# Revit family: S-757
name_source: partatom
category: Aparatos sanitarios
revit_build: Autodesk Revit 2015 (Build: 20140606_1530(x64)
units: mm (PartAtom-declared; Revit-internal decimal feet)

## types (12) — shared parameters
B = 52 mm
Comentarios de tipo = COMPATIBLE CON CERCOS VISTOS Y OCULTOS
Fabricante = Jimten
Modelo = S-757
URL = http://www.jimten.com

## per-type parameters (varying)
| type | A | Descripción | Material | Medida | Referencia | Rejilla |
| 50x350mm_CRYSTAL NEGRO | 340 mm  [stored 1.11549 ft] | REJILLA PARA CANALETA, CRYSTAL NEGRO, PARA CANALETA ANCHO 50 | Cristal templado (Negro) | 350mm x 50mm | 13533 | Cristal templado (Negro) |
| 50x550mm_CRYSTAL NEGRO | 540 mm  [stored 1.77165 ft] | REJILLA PARA CANALETA, CRYSTAL NEGRO, PARA CANALETA ANCHO 50 | Cristal templado (Negro) | 550mm x 50mm | 13553 | Cristal templado (Negro) |
| 50x650mm_CRYSTAL NEGRO | 640 mm  [stored 2.09974 ft] | REJILLA PARA CANALETA, CRYSTAL NEGRO, PARA CANALETA ANCHO 50 | Cristal templado (Negro) | 650mm x 50mm | 13563 | Cristal templado (Negro) |
| 50x750mm_CRYSTAL NEGRO | 740 mm  [stored 2.42782 ft] | REJILLA PARA CANALETA, CRYSTAL NEGRO, PARA CANALETA ANCHO 50 | Cristal templado (Negro) | 750mm x 50mm | 13573 | Cristal templado (Negro) |
| 50x850mm_CRYSTAL NEGRO | 840 mm  [stored 2.75591 ft] | REJILLA PARA CANALETA, CRYSTAL NEGRO, PARA CANALETA ANCHO 50 | Cristal templado (Negro) | 850mm x 50mm | 13583 | Cristal templado (Negro) |
| 50x950mm_CRYSTAL NEGRO | 940 mm  [stored 3.08399 ft] | REJILLA PARA CANALETA, CRYSTAL NEGRO, PARA CANALETA ANCHO 50 | Cristal templado (Negro) | 950mm x 50mm | 13593 | Cristal templado (Negro) |
| 50x350mm_CRYSTAL BLANCO | 340 mm  [stored 1.11549 ft] | REJILLA PARA CANALETA, CRYSTAL BLANCO, PARA CANALETA ANCHO 50 | Cristal templado (Blanco) | 350mm x 50mm | 13534 | Cristal templado (Blanco) |
| 50x550mm_CRYSTAL BLANCO | 540 mm  [stored 1.77165 ft] | REJILLA PARA CANALETA, CRYSTAL BLANCO, PARA CANALETA ANCHO 50 | Cristal templado (Blanco) | 550mm x 50mm | 13554 | Cristal templado (Blanco) |
| 50x650mm_CRYSTAL BLANCO | 640 mm  [stored 2.09974 ft] | REJILLA PARA CANALETA, CRYSTAL BLANCO, PARA CANALETA ANCHO 50 | Cristal templado (Blanco) | 650mm x 50mm | 13564 | Cristal templado (Blanco) |
| 50x750mm_CRYSTAL BLANCO | 740 mm  [stored 2.42782 ft] | REJILLA PARA CANALETA, CRYSTAL BLANCO, PARA CANALETA ANCHO 50 | Cristal templado (Blanco) | 750mm x 50mm | 13574 | Cristal templado (Blanco) |
| 50x850mm_CRYSTAL BLANCO | 840 mm  [stored 2.75591 ft] | REJILLA PARA CANALETA, CRYSTAL BLANCO, PARA CANALETA ANCHO 50 | Cristal templado (Blanco) | 850mm x 50mm | 13584 | Cristal templado (Blanco) |
| 50x950mm_CRYSTAL BLANCO | 940 mm  [stored 3.08399 ft] | REJILLA PARA CANALETA, CRYSTAL BLANCO, PARA CANALETA ANCHO 50 | Cristal templado (Blanco) | 950mm x 50 mm | 13594 | Cristal templado (Blanco) |

note: [stored X ft] marks values corroborated as IEEE doubles in the binary element streams (Revit-internal decimal feet)

## geometry (parser evidence)
native form markers: Blend x3, Sweep x3
no freeform markers — native parametric forms only
